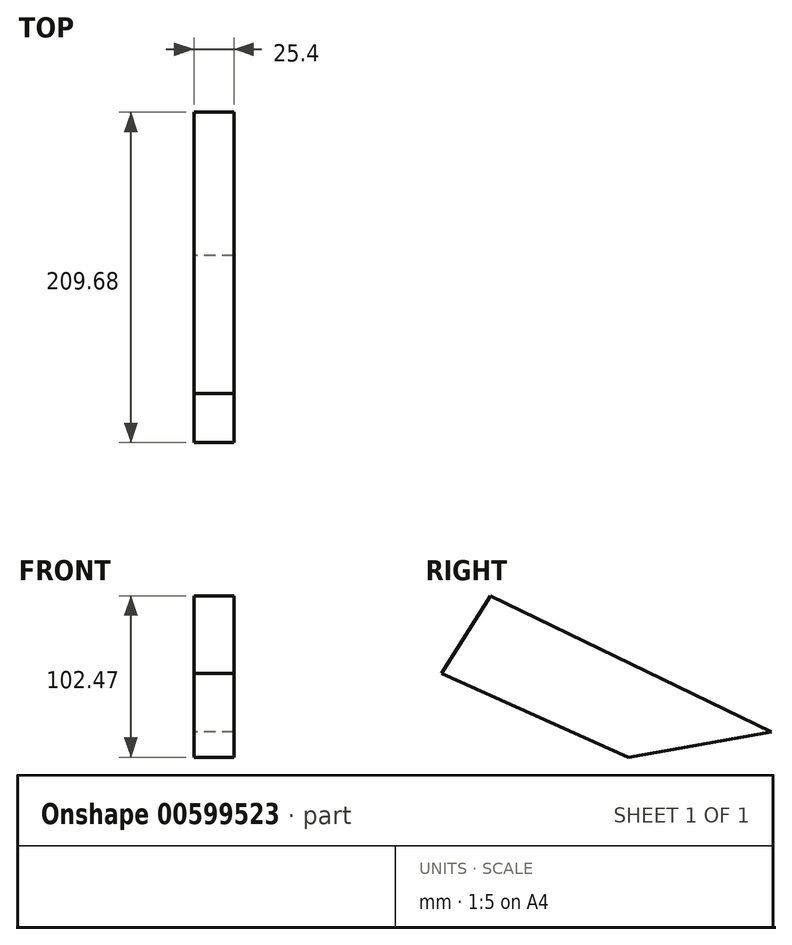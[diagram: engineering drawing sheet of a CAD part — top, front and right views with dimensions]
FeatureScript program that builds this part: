
annotation { "Feature Type Name" : "Feature", "Feature Type Description" : "" }
export const myFeature = defineFeature(function(context is Context, id is Id, definition is map)
    precondition{}
    {
        {
            var Q0;
            Q0=qCreatedBy(makeId("Right.planeOp"),FACE);
            var sketch = newSketch(context, id + "F0", { "sketchPlane" : qUnion([Q0])});
            skLineSegment(sketch, "E0", {"start": v(0, 0) * mm, "end": v(178.5, -86.25) * mm});
            skLineSegment(sketch, "E1", {"start": v(178.5, -86.25) * mm, "end": v(87.41, -102.47) * mm});
            skLineSegment(sketch, "E2", {"start": v(87.41, -102.47) * mm, "end": v(-31.18, -49.17) * mm});
            skLineSegment(sketch, "E3", {"start": v(-31.18, -49.17) * mm, "end": v(0, 0) * mm});
            skSolve(sketch);
        }
        {
            var Q0;
            Q0 = qSketchRegion(id + "F0", true);
            extrude(context, id + "F1", {"entities" : qUnion([Q0]), "depth" : 25.4 * mm, "offsetDistance" : 25.4 * mm});
        }
    });
